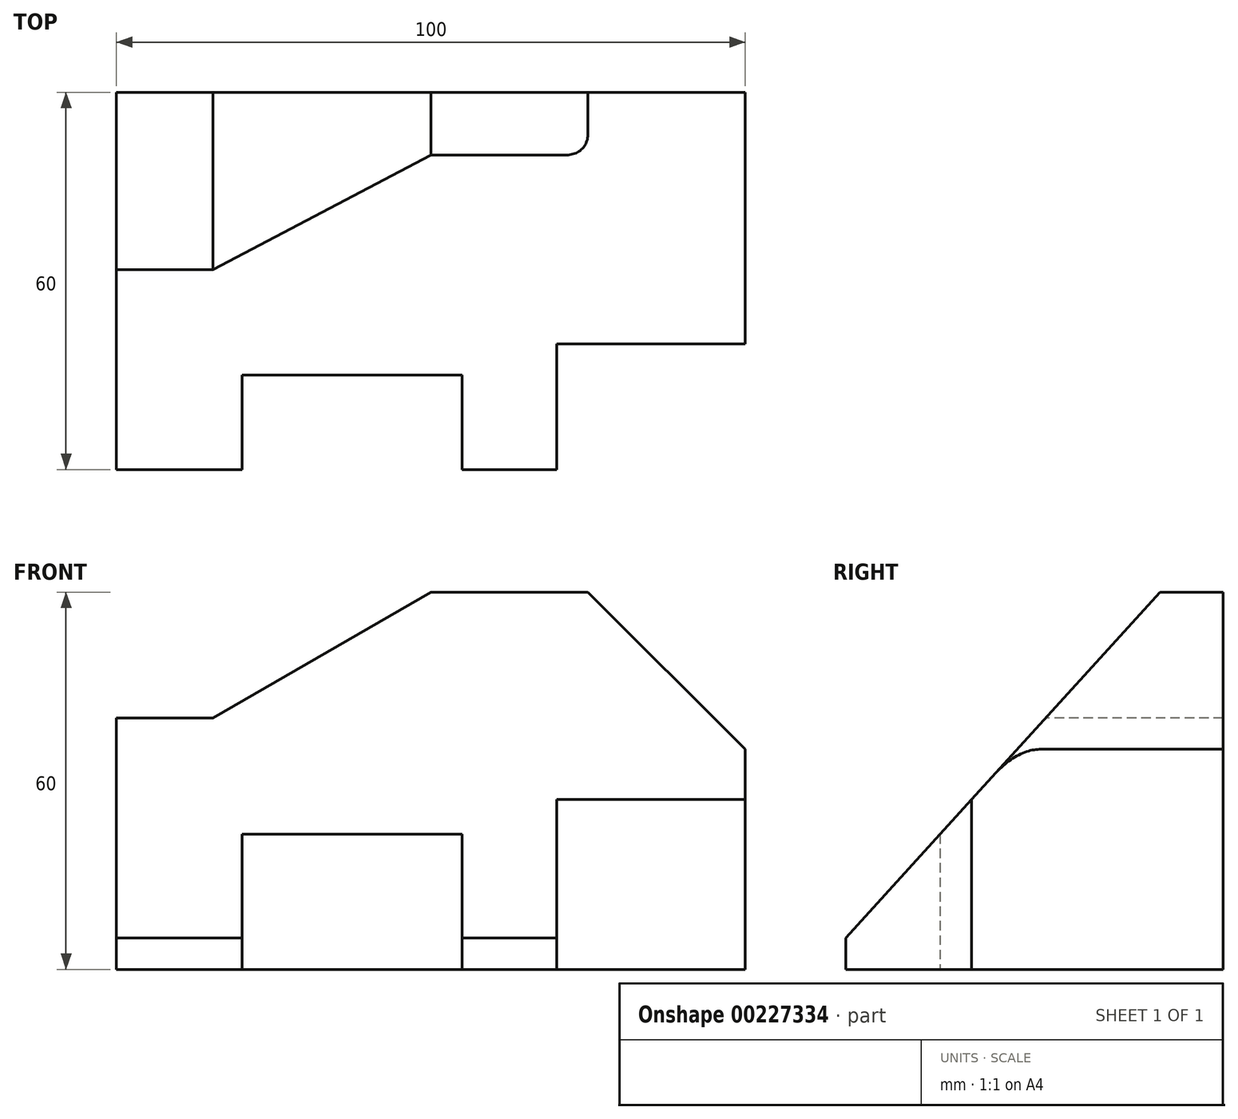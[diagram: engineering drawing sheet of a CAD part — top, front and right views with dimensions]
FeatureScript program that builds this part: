
annotation { "Feature Type Name" : "Feature", "Feature Type Description" : "" }
export const myFeature = defineFeature(function(context is Context, id is Id, definition is map)
    precondition{}
    {
        {
            var Q0;
            Q0=qCreatedBy(makeId("Top.planeOp"),FACE);
            var sketch = newSketch(context, id + "F0", { "sketchPlane" : qUnion([Q0])});
            skLineSegment(sketch, "E0.bottom", {"start": v(0, 0) * mm, "end": v(20, 0) * mm});
            skLineSegment(sketch, "E0.top", {"start": v(0, 60) * mm, "end": v(100, 60) * mm});
            skLineSegment(sketch, "E0.left", {"start": v(0, 0) * mm, "end": v(0, 60) * mm});
            skLineSegment(sketch, "E0.right", {"start": v(100, 20) * mm, "end": v(100, 60) * mm});
            skLineSegment(sketch, "E1.top", {"start": v(100, 20) * mm, "end": v(70, 20) * mm});
            skLineSegment(sketch, "E1.right", {"start": v(70, 0) * mm, "end": v(70, 20) * mm});
            skLineSegment(sketch, "E2.top", {"start": v(55, 15) * mm, "end": v(20, 15) * mm});
            skLineSegment(sketch, "E2.left", {"start": v(55, 0) * mm, "end": v(55, 15) * mm});
            skLineSegment(sketch, "E2.right", {"start": v(20, 0) * mm, "end": v(20, 15) * mm});
            skLineSegment(sketch, "E3.trimOffspring", {"start": v(55, 0) * mm, "end": v(70, 0) * mm});
            skSolve(sketch);
        }
        {
            var Q0;
            Q0 = qSketchRegion(id + "F0", true);
            extrude(context, id + "F1", {"entities" : qUnion([Q0]), "depth" : 60 * mm});
        }
        {
            var Q0;
            Q0=qCreatedBy(makeId("Front.planeOp"),FACE);
            var sketch = newSketch(context, id + "F2", { "sketchPlane" : qUnion([Q0])});
            skLineSegment(sketch, "E4.0", {"start": v(55, 60) * mm, "end": v(20, 60) * mm, "construction": true});
            skPoint(sketch, "E5.0", {"position": v(10, 60) * mm});
            skLineSegment(sketch, "E6.0", {"start": v(100, 60) * mm, "end": v(70, 60) * mm, "construction": true});
            skLineSegment(sketch, "E7.0", {"start": v(0, 60) * mm, "end": v(20, 60) * mm, "construction": true});
            skLineSegment(sketch, "E8.0", {"start": v(0, 60) * mm, "end": v(0, 0) * mm, "construction": true});
            skPoint(sketch, "E9.0", {"position": v(100, 30) * mm});
            skLineSegment(sketch, "E10.0", {"start": v(100, 60) * mm, "end": v(100, 0) * mm, "construction": true});
            skLineSegment(sketch, "E11", {"start": v(50, 60) * mm, "end": v(15.36, 40) * mm});
            skLineSegment(sketch, "E12", {"start": v(15.36, 40) * mm, "end": v(0, 40) * mm});
            skLineSegment(sketch, "E13", {"start": v(0, 40) * mm, "end": v(0, 60) * mm});
            skLineSegment(sketch, "E14", {"start": v(75, 60) * mm, "end": v(100, 35) * mm});
            skLineSegment(sketch, "E15", {"start": v(100, 35) * mm, "end": v(100, 60) * mm});
            skLineSegment(sketch, "E16", {"start": v(50, 60) * mm, "end": v(0, 60) * mm});
            skLineSegment(sketch, "E17", {"start": v(75, 60) * mm, "end": v(100, 60) * mm});
            skSolve(sketch);
        }
        {
            var Q0;
            Q0 = qSketchRegion(id + "F2", true);
            extrude(context, id + "F3", {"entities" : qUnion([Q0]), "operationType" : NewBodyOperationType.REMOVE, "endBound" : BoundingType.THROUGH_ALL, "oppositeDirection" : true, "depth" : 25 * mm});
        }
        {
            var Q0;
            Q0=qCreatedBy(makeId("Right.planeOp"),FACE);
            var sketch = newSketch(context, id + "F4", { "sketchPlane" : qUnion([Q0])});
            skLineSegment(sketch, "E18.0", {"start": v(60, 60) * mm, "end": v(20, 60) * mm, "construction": true});
            skLineSegment(sketch, "E19.0", {"start": v(0, 60) * mm, "end": v(20, 60) * mm, "construction": true});
            skLineSegment(sketch, "E20.0", {"start": v(0, 60) * mm, "end": v(0, 0) * mm, "construction": true});
            skLineSegment(sketch, "E21", {"start": v(50, 60) * mm, "end": v(0, 5) * mm});
            skLineSegment(sketch, "E22", {"start": v(0, 5) * mm, "end": v(0, 60) * mm});
            skLineSegment(sketch, "E23", {"start": v(0, 60) * mm, "end": v(50, 60) * mm});
            skSolve(sketch);
        }
        {
            var Q0;
            Q0 = qSketchRegion(id + "F4", true);
            extrude(context, id + "F5", {"entities" : qUnion([Q0]), "operationType" : NewBodyOperationType.REMOVE, "endBound" : BoundingType.THROUGH_ALL, "depth" : 25 * mm});
        }
        {
            var Q0;
            Q0=makeQuery(id+"F5.boolean.opBoolean","COPY",EDGE,{"derivedFrom":makeQuery(id+"F5.opExtrude","SWEPT_EDGE",EDGE,{"disambiguationData":[OSD([sQuery(id+"F4.wireOp",EDGE,"E21"),sQuery(id+"F4.wireOp",EDGE,"E23")])]})});
            var Q1;
            Q1=makeQuery(id+"F5.boolean.opBoolean","INTERSECT",EDGE,{"derivedFrom":[makeQuery(id+"F3.boolean.opBoolean","COPY",FACE,{"derivedFrom":makeQuery(id+"F3.opExtrude","SWEPT_FACE",FACE,{"disambiguationData":[OSD([sQuery(id+"F2.wireOp",EDGE,"E14")])]})}),makeQuery(id+"F5.opExtrude","SWEPT_FACE",FACE,{"disambiguationData":[OSD([sQuery(id+"F4.wireOp",EDGE,"E21")])]})]});
            fillet(context, id + "F6", {"entities" : qUnion([Q0, Q1]), "radius" : 5 * mm, "tangentPropagation" : true, "allowEdgeOverflow" : false});
        }
    });
